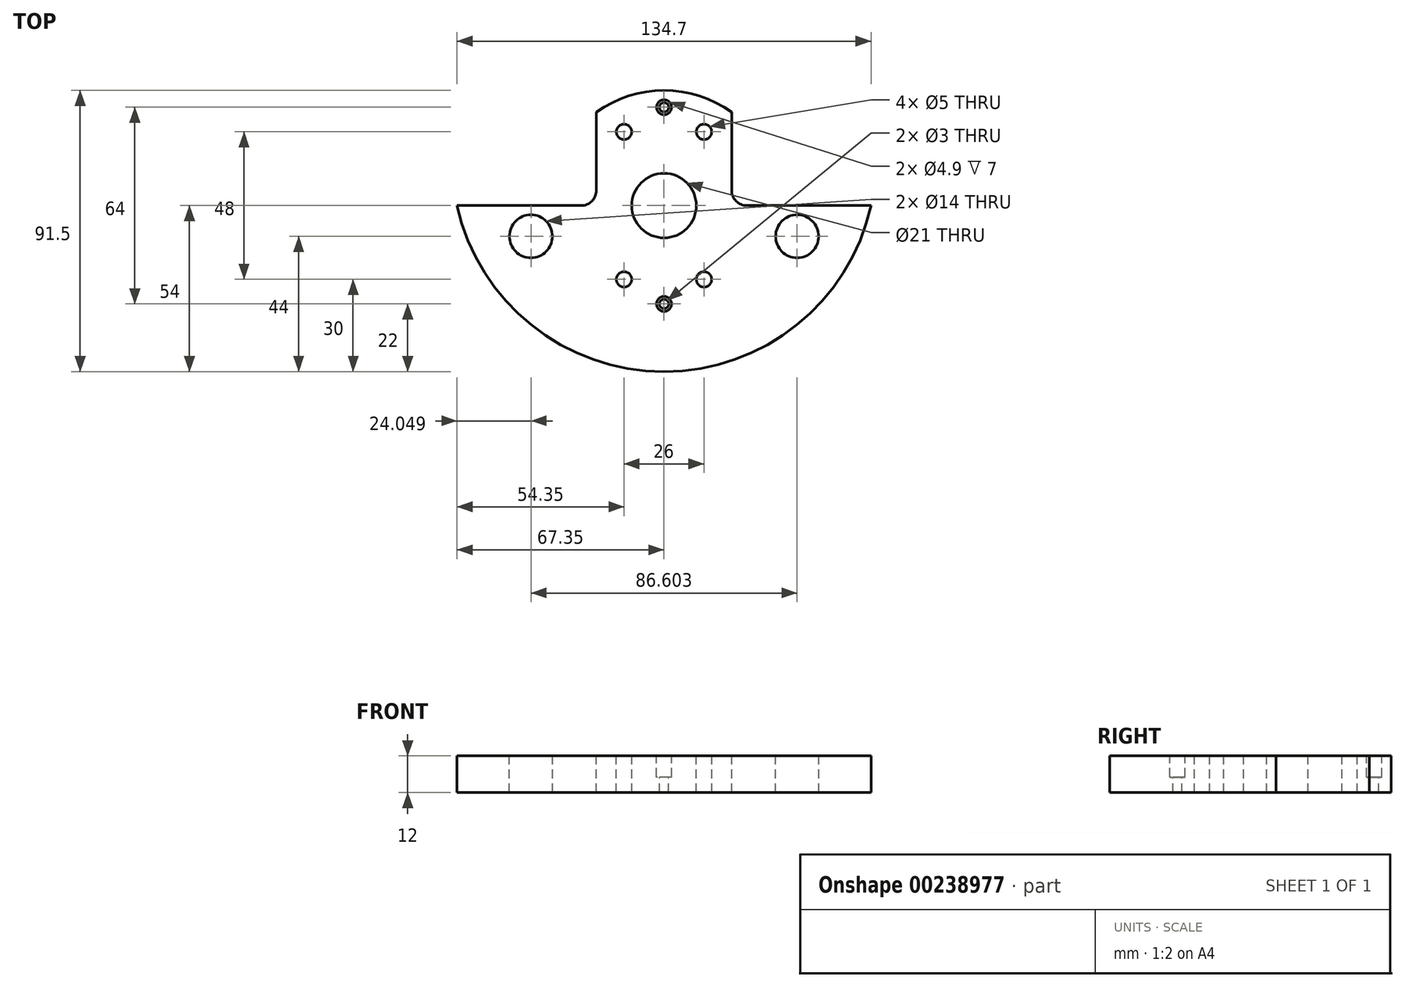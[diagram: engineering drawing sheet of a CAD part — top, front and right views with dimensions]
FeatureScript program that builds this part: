
annotation { "Feature Type Name" : "Feature", "Feature Type Description" : "" }
export const myFeature = defineFeature(function(context is Context, id is Id, definition is map)
    precondition{}
    {
        {
            var Q0;
            Q0=qCreatedBy(makeId("Top.planeOp"),FACE);
            var sketch = newSketch(context, id + "F0", { "sketchPlane" : qUnion([Q0])});
            skArc(sketch, "E0", {"start": v(-15.2, -3) * mm, "mid": v(0, -15.5) * mm, "end": v(15.2, -3) * mm});
            skArc(sketch, "E1", {"start": v(-66.61, -3) * mm, "mid": v(0, -54) * mm, "end": v(66.61, -3) * mm});
            skLineSegment(sketch, "E2", {"start": v(-66.61, -3) * mm, "end": v(-15.2, -3) * mm});
            skLineSegment(sketch, "E3.trimOffspring", {"start": v(15.2, -3) * mm, "end": v(66.61, -3) * mm});
            skCircle(sketch, "E4", {"center": v(-16, -15) * mm, "radius": 2.5 * mm, "construction": true});
            skCircle(sketch, "E5", {"center": v(0, -30) * mm, "radius": 2.5 * mm});
            skCircle(sketch, "E6", {"center": v(0, 15) * mm, "radius": 55 * mm, "construction": true});
            skCircle(sketch, "E7", {"center": v(-16, -25) * mm, "radius": 2.5 * mm});
            skCircle(sketch, "E8.MirrorC", {"center": v(16, -15) * mm, "radius": 2.5 * mm, "construction": true});
            skCircle(sketch, "E9.MirrorC", {"center": v(16, -25) * mm, "radius": 2.5 * mm});
            skCircle(sketch, "E10", {"center": v(0, 15) * mm, "radius": 50 * mm, "construction": true});
            skLineSegment(sketch, "E11.MirrorCS", {"start": v(0, 15) * mm, "end": v(78.85, -30.52) * mm, "construction": true});
            skCircle(sketch, "E12", {"center": v(43.3, -10) * mm, "radius": 20 * mm, "construction": true});
            skLineSegment(sketch, "E13.MirrorCS", {"start": v(0, 15) * mm, "end": v(-78.85, -30.52) * mm, "construction": true});
            skPoint(sketch, "E14.MirrorP", {"position": v(-43.3, -10) * mm});
            skSolve(sketch);
        }
        {
            var Q0;
            Q0=qCreatedBy(makeId("Top.planeOp"),FACE);
            cPlane(context, id + "F1", {"entities" : qUnion([Q0]), "cplaneType" : CPlaneType.OFFSET, "offset" : 19 * mm, "oppositeDirection" : true, "width" : 150 * mm, "height" : 150 * mm});
        }
        {
            var Q0;
            Q0=qCreatedBy(id+"F1.planeOp",FACE);
            var sketch = newSketch(context, id + "F2", { "sketchPlane" : qUnion([Q0])});
            skArc(sketch, "E15.0.1", {"start": v(-67.35, 0) * mm, "mid": v(-43.16, -38.83) * mm, "end": v(0, -54) * mm});
            skCircle(sketch, "E16.2", {"center": v(-13, -24) * mm, "radius": 2.5 * mm});
            skCircle(sketch, "E16.3", {"center": v(0, -32) * mm, "radius": 2.45 * mm, "construction": true});
            skLineSegment(sketch, "E17", {"start": v(-22, 30.37) * mm, "end": v(-22, 5) * mm});
            skCircle(sketch, "E18", {"center": v(0, 0) * mm, "radius": 10.5 * mm});
            skArc(sketch, "E19.trimOffspring", {"start": v(0, 37.5) * mm, "mid": v(-11.56, 35.67) * mm, "end": v(-22, 30.37) * mm});
            skCircle(sketch, "E20.MirrorC", {"center": v(13, -24) * mm, "radius": 2.5 * mm});
            skCircle(sketch, "E21.MirrorC", {"center": v(-13, 24) * mm, "radius": 2.5 * mm});
            skCircle(sketch, "E22.MirrorC", {"center": v(13, 24) * mm, "radius": 2.5 * mm});
            skCircle(sketch, "E23.MirrorC", {"center": v(0, 32) * mm, "radius": 2.45 * mm, "construction": true});
            skPoint(sketch, "E24.visualSharp", {"position": v(22, -3) * mm});
            skPoint(sketch, "E25.0", {"position": v(-43.3, -10) * mm});
            skPoint(sketch, "E26.0", {"position": v(43.3, -10) * mm});
            skLineSegment(sketch, "E27", {"start": v(-27, 0) * mm, "end": v(-67.35, 0) * mm});
            skArc(sketch, "E28.filletArc", {"start": v(-27, 0) * mm, "mid": v(-23.46, 1.46) * mm, "end": v(-22, 5) * mm});
            skPoint(sketch, "E29.startSnap0", {"position": v(0, 37.5) * mm});
            skPoint(sketch, "E29.endSnap0", {"position": v(0, -54) * mm});
            skArc(sketch, "E30.MirrorCS", {"start": v(27, 0) * mm, "mid": v(23.46, 1.46) * mm, "end": v(22, 5) * mm});
            skLineSegment(sketch, "E31.MirrorCS", {"start": v(27, 0) * mm, "end": v(67.35, 0) * mm});
            skArc(sketch, "E32.MirrorCS", {"start": v(67.35, 0) * mm, "mid": v(43.16, -38.83) * mm, "end": v(0, -54) * mm});
            skArc(sketch, "E33.MirrorCS", {"start": v(0, 37.5) * mm, "mid": v(11.56, 35.67) * mm, "end": v(22, 30.37) * mm});
            skLineSegment(sketch, "E34.MirrorCS", {"start": v(22, 30.37) * mm, "end": v(22, 5) * mm});
            skSolve(sketch);
        }
        {
            var Q0;
            Q0=qSketchRegion(id+"F2",true);
            extrude(context, id + "F3", {"entities" : qUnion([Q0]), "oppositeDirection" : true, "depth" : 12 * mm});
        }
        {
            var Q0;
            Q0=sQuery(id+"F2.wireOp",VERTEX,"E23.MirrorC.center");
            var Q1;
            Q1=sQuery(id+"F2.wireOp",VERTEX,"E16.3.center");
            var Q2;
            Q2=makeQuery(id+"F3.opExtrude","SWEPT_BODY",BODY,{"disambiguationData":[OSD([sQuery(id+"F2.wireOp",EDGE,"E15.0.0"),sQuery(id+"F2.wireOp",EDGE,"E15.0.1"),sQuery(id+"F2.wireOp",EDGE,"E15.0.2"),sQuery(id+"F2.wireOp",EDGE,"E16.2"),sQuery(id+"F2.wireOp",EDGE,"E17"),sQuery(id+"F2.wireOp",EDGE,"E18"),sQuery(id+"F2.wireOp",EDGE,"6ba06c93-55f0-47ca-b9f4-e73122be341e0.MirrorCS"),sQuery(id+"F2.wireOp",EDGE,"E19.trimOffspring"),sQuery(id+"F2.wireOp",EDGE,"E20.MirrorC"),sQuery(id+"F2.wireOp",EDGE,"E21.MirrorC"),sQuery(id+"F2.wireOp",EDGE,"E22.MirrorC"),sQuery(id+"F2.wireOp",EDGE,"dea0f098-3829-4f21-8c9d-72ae902d4f23.filletArc"),sQuery(id+"F2.wireOp",EDGE,"E24.filletArc")])]});
            hole(context, id + "F4", {"style" : HoleStyle.C_BORE, "endStyle" : HoleEndStyle.THROUGH, "holeDiameter" : 3 * mm, "cBoreDiameter" : 4.9 * mm, "cBoreDepth" : 7 * mm, "tappedDepth" : 12 * mm, "tapClearance" : 3, "startFromSketch" : true, "locations" : qUnion([Q0, Q1]), "scope" : qUnion([Q2])});
        }
        {
            var Q0;
            Q0=sQuery(id+"F0.wireOp",VERTEX,"E14.MirrorP");
            var Q1;
            Q1=sQuery(id+"F0.wireOp",VERTEX,"E12.center");
            var Q2;
            Q2=makeQuery(id+"F3.opExtrude","SWEPT_BODY",BODY,{"disambiguationData":[OSD([sQuery(id+"F2.wireOp",EDGE,"E15.0.1"),sQuery(id+"F2.wireOp",EDGE,"E16.2"),sQuery(id+"F2.wireOp",EDGE,"E17"),sQuery(id+"F2.wireOp",EDGE,"E18"),sQuery(id+"F2.wireOp",EDGE,"E19.trimOffspring"),sQuery(id+"F2.wireOp",EDGE,"E20.MirrorC"),sQuery(id+"F2.wireOp",EDGE,"E21.MirrorC"),sQuery(id+"F2.wireOp",EDGE,"E22.MirrorC"),sQuery(id+"F2.wireOp",EDGE,"E27"),sQuery(id+"F2.wireOp",EDGE,"E28.filletArc"),sQuery(id+"F2.wireOp",EDGE,"E30.MirrorCS"),sQuery(id+"F2.wireOp",EDGE,"E31.MirrorCS"),sQuery(id+"F2.wireOp",EDGE,"E32.MirrorCS"),sQuery(id+"F2.wireOp",EDGE,"E33.MirrorCS"),sQuery(id+"F2.wireOp",EDGE,"E34.MirrorCS")])]});
            hole(context, id + "F5", {"style" : HoleStyle.SIMPLE, "endStyle" : HoleEndStyle.THROUGH, "holeDiameter" : 14 * mm, "tappedDepth" : 12 * mm, "tapClearance" : 3, "startFromSketch" : true, "locations" : qUnion([Q0, Q1]), "scope" : qUnion([Q2])});
        }
    });
